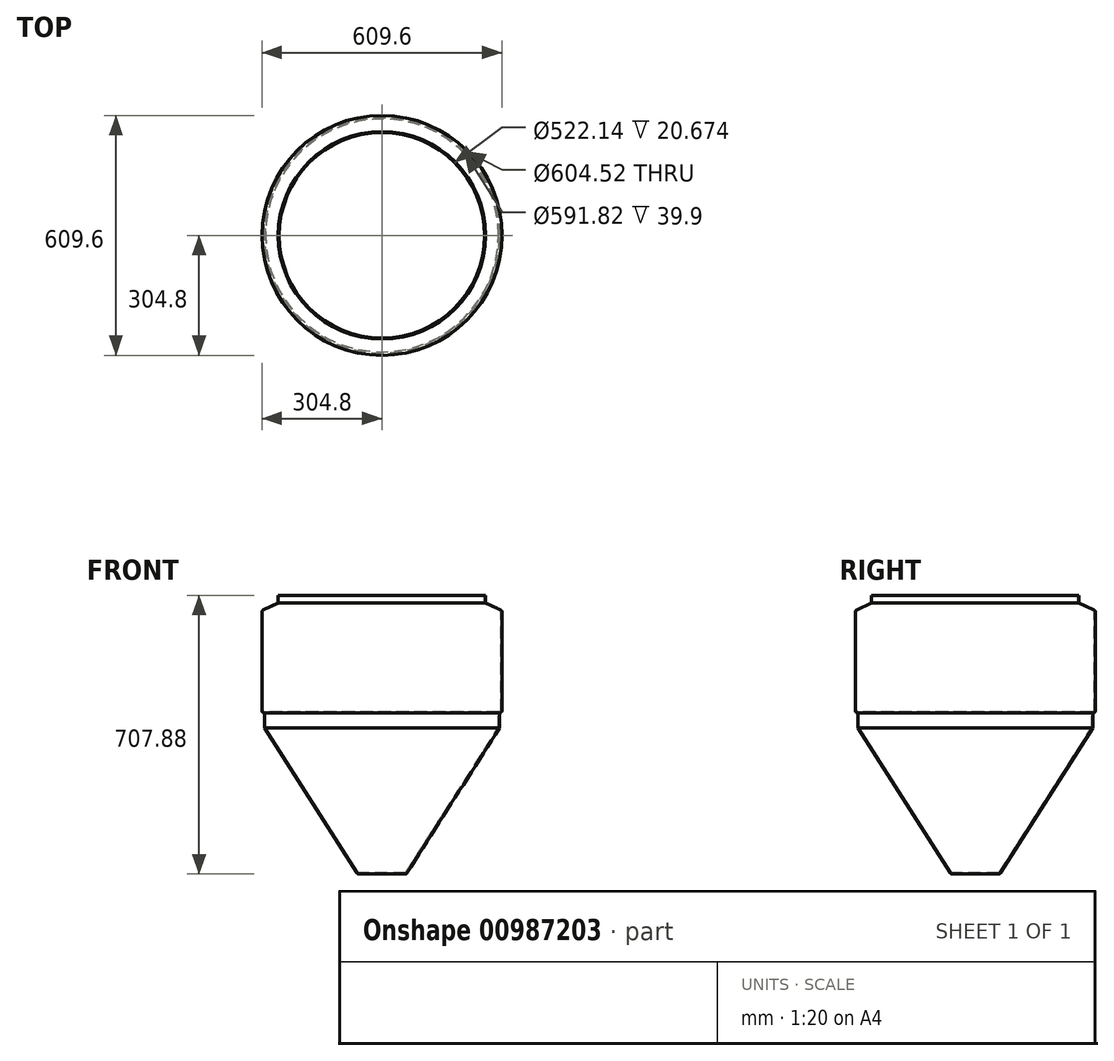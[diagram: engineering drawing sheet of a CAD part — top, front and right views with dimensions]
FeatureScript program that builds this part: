
annotation { "Feature Type Name" : "Feature", "Feature Type Description" : "" }
export const myFeature = defineFeature(function(context is Context, id is Id, definition is map)
    precondition{}
    {
        {
            var Q0;
            Q0=qCreatedBy(makeId("Front.planeOp"),FACE);
            var sketch = newSketch(context, id + "F0", { "sketchPlane" : qUnion([Q0])});
            skLineSegment(sketch, "E0", {"start": v(0, 0) * mm, "end": v(0, 249.46) * mm});
            skLineSegment(sketch, "E1", {"start": v(0, 0) * mm, "end": v(-58.84, 0) * mm});
            skLineSegment(sketch, "E2", {"start": v(-63.66, 2.65) * mm, "end": v(-298.45, 371.33) * mm});
            skLineSegment(sketch, "E3", {"start": v(-298.45, 371.33) * mm, "end": v(-298.45, 409.43) * mm});
            skLineSegment(sketch, "E4", {"start": v(-298.45, 409.43) * mm, "end": v(-299.09, 409.43) * mm});
            skLineSegment(sketch, "E5", {"start": v(-304.8, 415.15) * mm, "end": v(-304.8, 666.13) * mm});
            skLineSegment(sketch, "E6", {"start": v(-301.48, 671.32) * mm, "end": v(-263.61, 688.83) * mm});
            skLineSegment(sketch, "E7", {"start": v(-263.61, 688.83) * mm, "end": v(-263.61, 707.88) * mm});
            skLineSegment(sketch, "E8", {"start": v(-263.61, 707.88) * mm, "end": v(0, 707.88) * mm});
            skLineSegment(sketch, "E9", {"start": v(0, 707.88) * mm, "end": v(0, 249.46) * mm});
            skPoint(sketch, "E10.visualSharp", {"position": v(-304.8, 409.43) * mm});
            skArc(sketch, "E10.filletArc", {"start": v(-304.8, 415.15) * mm, "mid": v(-303.13, 411.1) * mm, "end": v(-299.09, 409.43) * mm});
            skPoint(sketch, "E11.visualSharp", {"position": v(-61.98, 0) * mm});
            skArc(sketch, "E11.filletArc", {"start": v(-63.66, 2.65) * mm, "mid": v(-61.59, 0.7) * mm, "end": v(-58.84, 0) * mm});
            skPoint(sketch, "E12.visualSharp", {"position": v(-304.8, 669.78) * mm});
            skArc(sketch, "E12.filletArc", {"start": v(-301.48, 671.32) * mm, "mid": v(-303.9, 669.2) * mm, "end": v(-304.8, 666.13) * mm});
            skSolve(sketch);
        }
        {
            var Q0;
            Q0=makeQuery(id+"F0.imprint","IMPRINT",FACE,{"disambiguationData":[TD([[makeQuery(id+"F0.imprint","IMPRINT",EDGE,{"derivedFrom":sQuery(id+"F0.wireOp",EDGE,"E0")}),1.0]])]});
            var Q1;
            Q1=sQuery(id+"F0.wireOp",EDGE,"E9");
            revolve(context, id + "F1", {"surfaceOperationType" : NewSurfaceOperationType.NEW, "entities" : qUnion([Q0]), "axis" : qUnion([Q1]), "revolveType" : RevolveType.FULL});
        }
        {
            var Q0;
            Q0=makeQuery(id+"F1.opRevolve","SWEPT_FACE",FACE,{"disambiguationData":[OSD([sQuery(id+"F0.wireOp",EDGE,"E8")])]});
            shell(context, id + "F2", {"entities" : qUnion([Q0]), "thickness" : 2.54 * mm});
        }
    });
